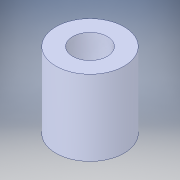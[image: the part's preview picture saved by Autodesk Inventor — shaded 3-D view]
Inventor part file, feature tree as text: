
AUTODESK INVENTOR PART (.ipt)
format: ipt  version: 2018 (Build 220112000, 112)  size: 110,080 bytes
history: native  units: in
note: dims shown in document units (in); Inventor stores cm internally (conversion verified against a paired STEP export)
features: extrude x1, sketch x1
ambient origin geometry x8: Origin, YZ Plane, XZ Plane, XY Plane, X Axis, Y Axis, Z Axis, Center Point
bodies: Solid1 (feature_tree), Body1 (feature_tree)
feature tree (2):
  extrude  "Extrusion1"  [1 undecoded]
  sketch  "Sketch1"  dims[d0=0.02in d1=0.0in]
note: 1 required parameter value undecoded (feature->parameter linkage not recoverable at this tier; creation-order binding heuristic only, values carry confidence <= 0.55)
